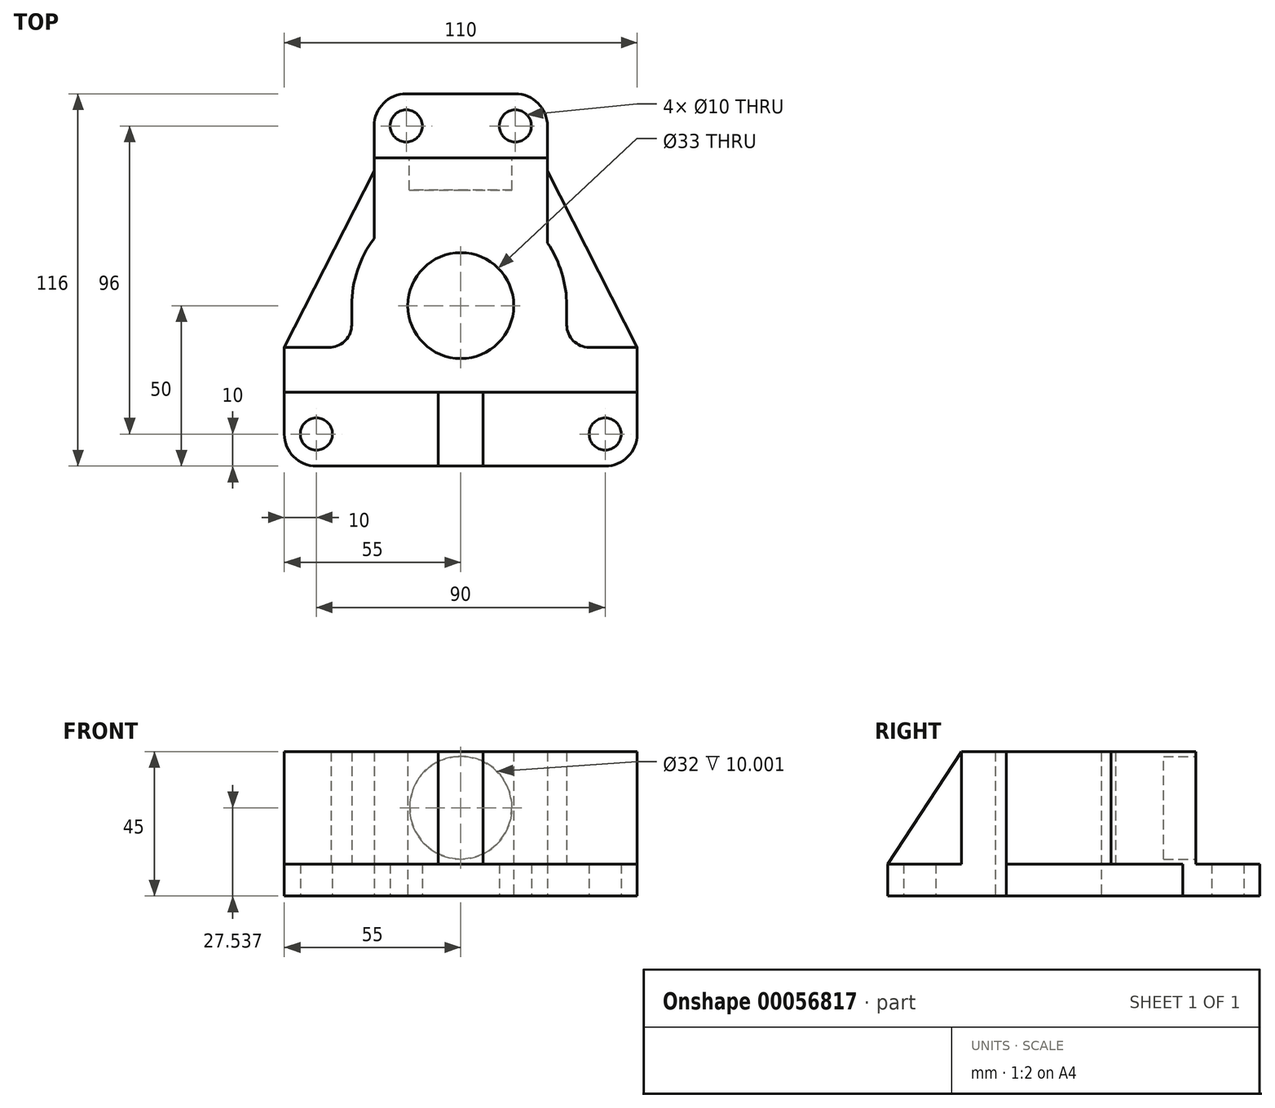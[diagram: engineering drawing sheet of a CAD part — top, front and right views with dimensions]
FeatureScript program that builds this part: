
annotation { "Feature Type Name" : "Feature", "Feature Type Description" : "" }
export const myFeature = defineFeature(function(context is Context, id is Id, definition is map)
    precondition{}
    {
        {
            var Q0;
            Q0=qCreatedBy(makeId("Top.planeOp"),FACE);
            var sketch = newSketch(context, id + "F0", { "sketchPlane" : qUnion([Q0])});
            skLineSegment(sketch, "E0.rect.bottom", {"start": v(17, 66) * mm, "end": v(-17, 66) * mm});
            skLineSegment(sketch, "E0.rect.left", {"start": v(27, 56) * mm, "end": v(27, 19.56) * mm});
            skLineSegment(sketch, "E0.rect.right", {"start": v(-27, 56) * mm, "end": v(-27, 20.96) * mm});
            skPoint(sketch, "E0.rect.middle", {"position": v(0, 0) * mm});
            skLineSegment(sketch, "E1.rect.bottom", {"start": v(45, -50) * mm, "end": v(-45, -50) * mm});
            skLineSegment(sketch, "E1.rect.left", {"start": v(55, -40) * mm, "end": v(55, -13) * mm});
            skLineSegment(sketch, "E1.rect.right", {"start": v(-55, -40) * mm, "end": v(-55, -13) * mm});
            skPoint(sketch, "E2.visualSharp", {"position": v(-55, -50) * mm});
            skArc(sketch, "E2.filletArc", {"start": v(-55, -40) * mm, "mid": v(-52.07, -47.07) * mm, "end": v(-45, -50) * mm});
            skPoint(sketch, "E3.visualSharp", {"position": v(55, -50) * mm});
            skArc(sketch, "E3.filletArc", {"start": v(45, -50) * mm, "mid": v(52.07, -47.07) * mm, "end": v(55, -40) * mm});
            skPoint(sketch, "E4", {"position": v(-55, -13) * mm});
            skPoint(sketch, "E5", {"position": v(55, -13) * mm});
            skPoint(sketch, "E6", {"position": v(0, -50) * mm});
            skPoint(sketch, "E7", {"position": v(0, 66) * mm});
            skPoint(sketch, "E8.visualSharp", {"position": v(-27, 66) * mm});
            skArc(sketch, "E8.filletArc", {"start": v(-17, 66) * mm, "mid": v(-24.07, 63.07) * mm, "end": v(-27, 56) * mm});
            skPoint(sketch, "E9.visualSharp", {"position": v(27, 66) * mm});
            skArc(sketch, "E9.filletArc", {"start": v(27, 56) * mm, "mid": v(24.07, 63.07) * mm, "end": v(17, 66) * mm});
            skLineSegment(sketch, "E10", {"start": v(40, -13) * mm, "end": v(55, -13) * mm});
            skCircle(sketch, "E11", {"center": v(0, 0) * mm, "radius": 16.5 * mm});
            skLineSegment(sketch, "E12", {"start": v(-34, -6.02) * mm, "end": v(-34, 0) * mm});
            skLineSegment(sketch, "E13", {"start": v(33, 0) * mm, "end": v(33, -6) * mm});
            skArc(sketch, "E14.filletArc", {"start": v(-40.46, -13) * mm, "mid": v(-35.86, -10.78) * mm, "end": v(-34, -6.02) * mm});
            skArc(sketch, "E15.filletArc", {"start": v(33, -6) * mm, "mid": v(35.05, -10.95) * mm, "end": v(40, -13) * mm});
            skPoint(sketch, "E16", {"position": v(-55, -27) * mm});
            skPoint(sketch, "E17", {"position": v(55, -27) * mm});
            skCircle(sketch, "E18", {"center": v(-45, -40) * mm, "radius": 5 * mm});
            skCircle(sketch, "E19", {"center": v(45, -40) * mm, "radius": 5 * mm});
            skCircle(sketch, "E20", {"center": v(-17, 56) * mm, "radius": 5 * mm});
            skCircle(sketch, "E21", {"center": v(17, 56) * mm, "radius": 5 * mm});
            skLineSegment(sketch, "E22", {"start": v(-55, -13) * mm, "end": v(-40.46, -13) * mm});
            skLineSegment(sketch, "E23", {"start": v(-55, -27) * mm, "end": v(55, -27) * mm});
            skArc(sketch, "E24", {"start": v(-27, 20.96) * mm, "mid": v(-32.2, 11.05) * mm, "end": v(-34, 0) * mm});
            skArc(sketch, "E25", {"start": v(33, 0) * mm, "mid": v(31.47, 10.23) * mm, "end": v(27, 19.56) * mm});
            skPoint(sketch, "E26", {"position": v(-6, -50) * mm});
            skPoint(sketch, "E27", {"position": v(6, -50) * mm});
            skLineSegment(sketch, "E28", {"start": v(-6, -50) * mm, "end": v(-6, -27) * mm});
            skLineSegment(sketch, "E29", {"start": v(6, -50) * mm, "end": v(6, -27) * mm});
            skPoint(sketch, "E30", {"position": v(-27, 46) * mm});
            skPoint(sketch, "E31", {"position": v(27, 46) * mm});
            skLineSegment(sketch, "E32", {"start": v(-27, 46) * mm, "end": v(27, 46) * mm});
            skPoint(sketch, "E33", {"position": v(-27, 42) * mm});
            skPoint(sketch, "E34", {"position": v(27, 42) * mm});
            skLineSegment(sketch, "E35", {"start": v(-55, -13) * mm, "end": v(-27, 42) * mm});
            skLineSegment(sketch, "E36", {"start": v(55, -13) * mm, "end": v(27, 42) * mm});
            skLineSegment(sketch, "E37", {"start": v(55, -13) * mm, "end": v(55, 42) * mm, "construction": true});
            skLineSegment(sketch, "E38", {"start": v(55, 42) * mm, "end": v(27, 42) * mm, "construction": true});
            skLineSegment(sketch, "E39", {"start": v(-55, -13) * mm, "end": v(-55, 42) * mm, "construction": true});
            skLineSegment(sketch, "E40", {"start": v(-55, 42) * mm, "end": v(-27, 42) * mm, "construction": true});
            skSolve(sketch);
        }
        {
            var Q0;
            Q0=makeQuery(id+"F0.imprint","IMPRINT",FACE,{"disambiguationData":[TD([[makeQuery(id+"F0.imprint","IMPRINT",EDGE,{"derivedFrom":sQuery(id+"F0.wireOp",EDGE,"E0.rect.bottom")}),1.0]])]});
            var Q1;
            {var subQ12=sQuery(id+"F0.wireOp",EDGE,"E10");Q1=makeQuery(id+"F0.imprint","IMPRINT",FACE,{"disambiguationData":[TD([[makeQuery(id+"F0.imprint","IMPRINT",EDGE,{"derivedFrom":subQ12}),-1.0]])]});}
            var Q2;
            Q2=makeQuery(id+"F0.imprint","IMPRINT",FACE,{"disambiguationData":[TD([[makeQuery(id+"F0.imprint","IMPRINT",EDGE,{"derivedFrom":sQuery(id+"F0.wireOp",EDGE,"E10")}),1.0]])]});
            var Q3;
            {var subQ0=sQuery(id+"F0.wireOp",EDGE,"E2.filletArc");Q3=makeQuery(id+"F0.imprint","IMPRINT",FACE,{"disambiguationData":[TD([[makeQuery(id+"F0.imprint","IMPRINT",EDGE,{"derivedFrom":subQ0}),1.0]])]});}
            var Q4;
            {var subQ0=sQuery(id+"F0.wireOp",EDGE,"E3.filletArc");Q4=makeQuery(id+"F0.imprint","IMPRINT",FACE,{"disambiguationData":[TD([[makeQuery(id+"F0.imprint","IMPRINT",EDGE,{"derivedFrom":subQ0}),1.0]])]});}
            var Q5;
            Q5=makeQuery(id+"F0.imprint","IMPRINT",FACE,{"disambiguationData":[TD([[makeQuery(id+"F0.imprint","IMPRINT",EDGE,{"derivedFrom":sQuery(id+"F0.wireOp",EDGE,"E12")}),1.0]])]});
            extrude(context, id + "F1", {"entities" : qUnion([Q0, Q1, Q2, Q3, Q4, Q5]), "depth" : 10 * mm});
        }
        {
            var Q0;
            {var subQ9=sQuery(id+"F0.wireOp",EDGE,"E10");Q0=makeQuery(id+"F0.imprint","IMPRINT",FACE,{"disambiguationData":[TD([[makeQuery(id+"F0.imprint","IMPRINT",EDGE,{"derivedFrom":subQ9}),-1.0]])]});}
            extrude(context, id + "F2", {"entities" : qUnion([Q0]), "operationType" : NewBodyOperationType.ADD, "depth" : 45 * mm});
        }
        {
            var Q0;
            Q0=qCreatedBy(makeId("Front.planeOp"),FACE);
            cPlane(context, id + "F3", {"entities" : qUnion([Q0]), "cplaneType" : CPlaneType.OFFSET, "offset" : 46 * mm, "oppositeDirection" : true, "width" : 150 * mm, "height" : 150 * mm});
        }
        {
            var Q0;
            Q0=qCreatedBy(id+"F3.planeOp",FACE);
            var sketch = newSketch(context, id + "F4", { "sketchPlane" : qUnion([Q0])});
            skPoint(sketch, "E41", {"position": v(0, -1.1) * mm});
            skCircle(sketch, "E42", {"center": v(0, 27.54) * mm, "radius": 16 * mm});
            skSolve(sketch);
        }
        {
            var Q0;
            Q0=makeQuery(id+"F4.imprint","IMPRINT",FACE,{"disambiguationData":[TD([[makeQuery(id+"F4.imprint","IMPRINT",EDGE,{"derivedFrom":sQuery(id+"F4.wireOp",EDGE,"E42")}),1.0]])]});
            extrude(context, id + "F5", {"entities" : qUnion([Q0]), "operationType" : NewBodyOperationType.REMOVE, "depth" : 10 * mm});
        }
        {
            var Q0;
            Q0=qCreatedBy(makeId("Right.planeOp"),FACE);
            var sketch = newSketch(context, id + "F6", { "sketchPlane" : qUnion([Q0])});
            skLineSegment(sketch, "E43", {"start": v(-50, 10) * mm, "end": v(-27, 45) * mm});
            skLineSegment(sketch, "E44", {"start": v(-27, 45) * mm, "end": v(-27, 10) * mm});
            skLineSegment(sketch, "E45", {"start": v(-27, 10) * mm, "end": v(-50, 10) * mm});
            skSolve(sketch);
        }
        {
            var Q0;
            Q0=makeQuery(id+"F6.imprint","IMPRINT",FACE,{"disambiguationData":[TD([[makeQuery(id+"F6.imprint","IMPRINT",EDGE,{"derivedFrom":sQuery(id+"F6.wireOp",EDGE,"E43")}),-1.0]])]});
            extrude(context, id + "F7", {"entities" : qUnion([Q0]), "operationType" : NewBodyOperationType.ADD, "depth" : 7 * mm});
        }
        {
            var Q0;
            Q0 = qSketchRegion(id + "F6", true);
            extrude(context, id + "F8", {"entities" : qUnion([Q0]), "operationType" : NewBodyOperationType.ADD, "oppositeDirection" : true, "depth" : 7 * mm});
        }
        {
            var Q0;
            {var subQ0=sQuery(id+"F0.wireOp",EDGE,"E28");Q0=makeQuery(id+"F0.imprint","IMPRINT",FACE,{"disambiguationData":[TD([[makeQuery(id+"F0.imprint","IMPRINT",EDGE,{"derivedFrom":subQ0}),-1.0]])]});}
            extrude(context, id + "F9", {"entities" : qUnion([Q0]), "operationType" : NewBodyOperationType.ADD, "depth" : 10 * mm});
        }
    });
